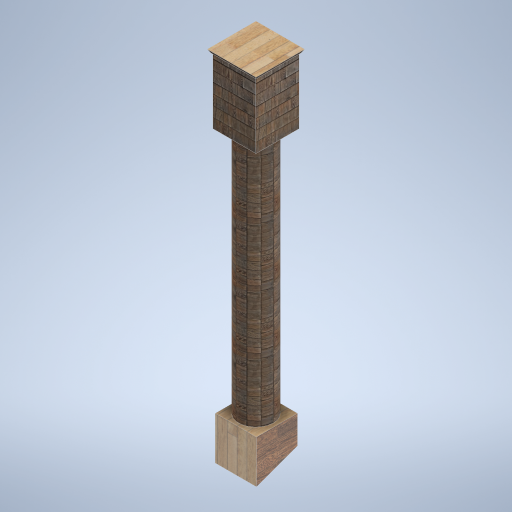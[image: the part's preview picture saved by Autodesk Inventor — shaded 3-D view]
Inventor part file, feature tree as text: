
AUTODESK INVENTOR PART (.ipt)
format: ipt  version: 2024.2 (Build 282272000, 272)  size: 350,720 bytes
history: native  units: in
note: dims shown in document units (in); Inventor stores cm internally (conversion verified against a paired STEP export)
features: sketch x5, other x3, plane x1
ambient origin geometry x8: Origin, YZ Plane, XZ Plane, XY Plane, X Axis, Y Axis, Z Axis, Center Point
bodies: Solid1 (feature_tree)
feature tree (9):
  other  "side_pillar_01.ipt"
  other  "Solid1::side_pillar_01.ipt"
  other  "TaggingFeature1"
  sketch  "Sketch1"  dims[d0=0.3937in]
  sketch  "Sketch2"
  sketch  "Sketch3"
  sketch  "Sketch4"
  sketch  "Sketch5"
  plane  "Work Plane3"
